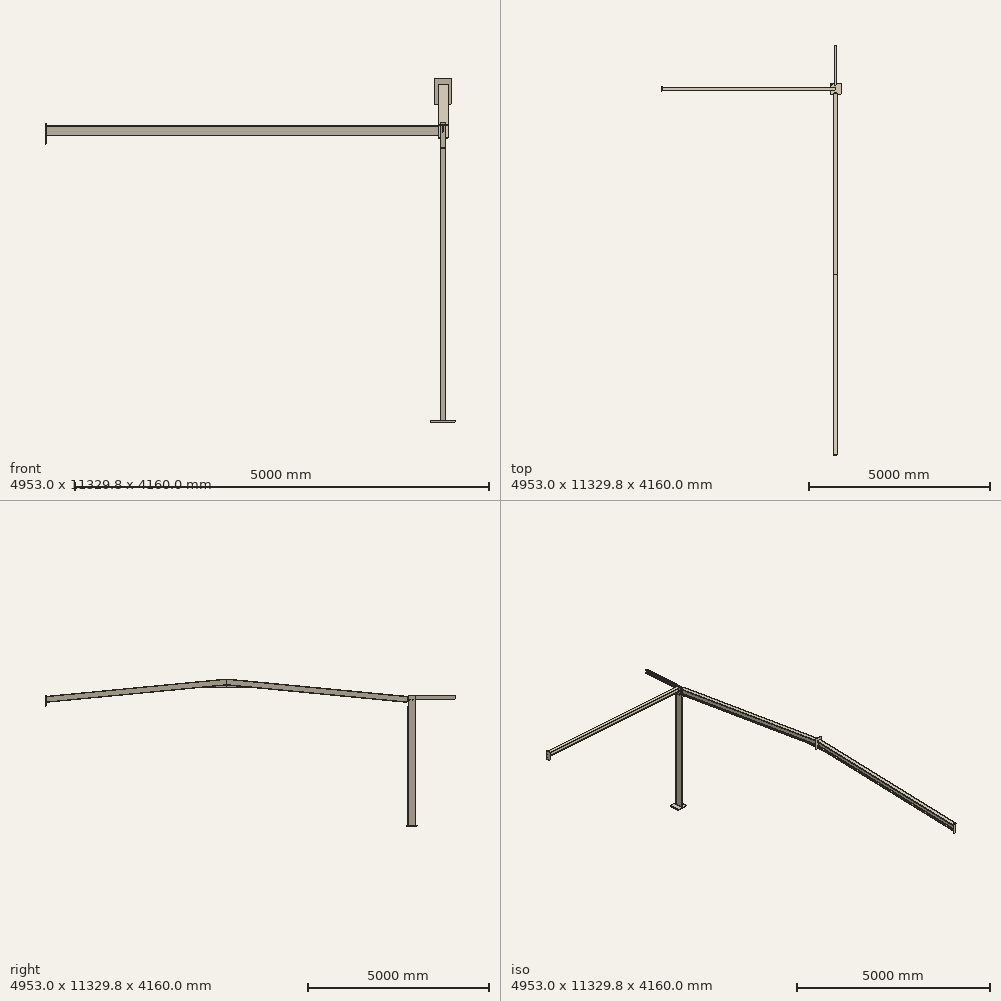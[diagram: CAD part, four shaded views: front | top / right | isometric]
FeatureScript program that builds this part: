
annotation { "Feature Type Name" : "Feature", "Feature Type Description" : "" }
export const myFeature = defineFeature(function(context is Context, id is Id, definition is map)
    precondition{}
    {
        {
            var Q0;
            Q0=qCreatedBy(makeId("Right.planeOp"),FACE);
            var sketch = newSketch(context, id + "F0", { "sketchPlane" : qUnion([Q0])});
            skLineSegment(sketch, "E0", {"start": v(-363, 0) * mm, "end": v(480.55, 0) * mm, "construction": true});
            skLineSegment(sketch, "E1", {"start": v(0, 0) * mm, "end": v(-4976.98, -479.23) * mm, "construction": true});
            skLineSegment(sketch, "E2", {"start": v(0, 0) * mm, "end": v(-23.08, 239.68) * mm, "construction": true});
            skLineSegment(sketch, "E3", {"start": v(0, 0) * mm, "end": v(4976.98, -479.23) * mm, "construction": true});
            skLineSegment(sketch, "E4", {"start": v(0, 0) * mm, "end": v(23.08, 239.68) * mm, "construction": true});
            skLineSegment(sketch, "E5.0", {"start": v(4976.98, -479.23) * mm, "end": v(5000.06, -239.54) * mm});
            skLineSegment(sketch, "E6.0", {"start": v(-4976.98, -479.23) * mm, "end": v(-5000.06, -239.54) * mm});
            skPoint(sketch, "E7.orphan", {"position": v(480.55, -46.27) * mm});
            skSolve(sketch);
        }
        {
            var Q0;
            Q0=sQuery(id+"F0.wireOp",EDGE,"E2");
            cPlane(context, id + "F1", {"entities" : qUnion([Q0]), "cplaneType" : CPlaneType.LINE_ANGLE, "offset" : 25 * mm, "angle" : 90 * degree, "width" : 150 * mm, "height" : 150 * mm});
        }
        {
            var Q0;
            Q0=sQuery(id+"F0.wireOp",EDGE,"E4");
            cPlane(context, id + "F2", {"entities" : qUnion([Q0]), "cplaneType" : CPlaneType.LINE_ANGLE, "offset" : 25 * mm, "angle" : 90 * degree, "width" : 150 * mm, "height" : 150 * mm});
        }
        {
            var Q0;
            Q0=qCreatedBy(makeId("Front.planeOp"),FACE);
            var sketch = newSketch(context, id + "F3", { "sketchPlane" : qUnion([Q0])});
            skLineSegment(sketch, "E8.bottom", {"start": v(100, -160) * mm, "end": v(-100, -160) * mm});
            skLineSegment(sketch, "E8.top", {"start": v(100, 160) * mm, "end": v(-100, 160) * mm});
            skLineSegment(sketch, "E8.left", {"start": v(100, -160) * mm, "end": v(100, 160) * mm});
            skLineSegment(sketch, "E8.right", {"start": v(-100, -160) * mm, "end": v(-100, 160) * mm});
            skPoint(sketch, "E8.middle", {"position": v(0, 0) * mm});
            skSolve(sketch);
        }
        {
            var Q0;
            Q0=qCreatedBy(id+"F1.planeOp",FACE);
            cPlane(context, id + "F4", {"entities" : qUnion([Q0]), "cplaneType" : CPlaneType.OFFSET, "offset" : 5000 * mm, "oppositeDirection" : true, "width" : 150 * mm, "height" : 150 * mm});
        }
        {
            var Q0;
            Q0=qCreatedBy(id+"F2.planeOp",FACE);
            cPlane(context, id + "F5", {"entities" : qUnion([Q0]), "cplaneType" : CPlaneType.OFFSET, "offset" : 5020 * mm, "width" : 150 * mm, "height" : 150 * mm});
        }
        {
            var Q0;
            Q0=qCreatedBy(id+"F5.planeOp",FACE);
            var sketch = newSketch(context, id + "F6", { "sketchPlane" : qUnion([Q0])});
            skLineSegment(sketch, "E9", {"start": v(60, 82.46) * mm, "end": v(-60, 82.46) * mm});
            skLineSegment(sketch, "E10", {"start": v(-60, 82.46) * mm, "end": v(-60, 72.46) * mm});
            skLineSegment(sketch, "E11", {"start": v(-60, 72.46) * mm, "end": v(-5, 72.46) * mm});
            skLineSegment(sketch, "E12", {"start": v(-5, 72.46) * mm, "end": v(-5, -72.46) * mm});
            skLineSegment(sketch, "E13", {"start": v(-5, -72.46) * mm, "end": v(-60, -72.46) * mm});
            skLineSegment(sketch, "E14", {"start": v(-60, -72.46) * mm, "end": v(-60, -82.46) * mm});
            skLineSegment(sketch, "E15", {"start": v(-60, -82.46) * mm, "end": v(60, -82.46) * mm});
            skLineSegment(sketch, "E16", {"start": v(60, -82.46) * mm, "end": v(60, -72.46) * mm});
            skLineSegment(sketch, "E17", {"start": v(60, -72.46) * mm, "end": v(5, -72.46) * mm});
            skLineSegment(sketch, "E18", {"start": v(5, -72.46) * mm, "end": v(5, 72.46) * mm});
            skLineSegment(sketch, "E19", {"start": v(5, 72.46) * mm, "end": v(60, 72.46) * mm});
            skLineSegment(sketch, "E20", {"start": v(60, 72.46) * mm, "end": v(60, 82.46) * mm});
            skPoint(sketch, "E21", {"position": v(-322.82, 17) * mm});
            skLineSegment(sketch, "E22", {"start": v(-5, 0) * mm, "end": v(5, 0) * mm, "construction": true});
            skPoint(sketch, "E23", {"position": v(0, 0) * mm});
            skSolve(sketch);
        }
        {
            var Q0;
            Q0=qSketchRegion(id+"F3",true);
            extrude(context, id + "F7", {"entities" : qUnion([Q0]), "depth" : 10 * mm});
        }
        {
            var Q0;
            Q0=qSketchRegion(id+"F6",true);
            extrude(context, id + "F8", {"entities" : qUnion([Q0]), "operationType" : NewBodyOperationType.ADD, "endBound" : BoundingType.UP_TO_NEXT, "oppositeDirection" : true, "depth" : 25 * mm});
        }
        {
            var Q0;
            Q0=qCreatedBy(id+"F4.planeOp",FACE);
            var sketch = newSketch(context, id + "F9", { "sketchPlane" : qUnion([Q0])});
            skLineSegment(sketch, "E24", {"start": v(60, 82.46) * mm, "end": v(-60, 82.46) * mm});
            skLineSegment(sketch, "E25", {"start": v(-60, 82.46) * mm, "end": v(-60, 72.46) * mm});
            skLineSegment(sketch, "E26", {"start": v(-60, 72.46) * mm, "end": v(-5, 72.46) * mm});
            skLineSegment(sketch, "E27", {"start": v(-5, 72.46) * mm, "end": v(-5, -72.46) * mm});
            skLineSegment(sketch, "E28", {"start": v(-5, -72.46) * mm, "end": v(-60, -72.46) * mm});
            skLineSegment(sketch, "E29", {"start": v(-60, -72.46) * mm, "end": v(-60, -82.46) * mm});
            skLineSegment(sketch, "E30", {"start": v(-60, -82.46) * mm, "end": v(60, -82.46) * mm});
            skLineSegment(sketch, "E31", {"start": v(60, -82.46) * mm, "end": v(60, -72.46) * mm});
            skLineSegment(sketch, "E32", {"start": v(60, -72.46) * mm, "end": v(5, -72.46) * mm});
            skLineSegment(sketch, "E33", {"start": v(5, -72.46) * mm, "end": v(5, 72.46) * mm});
            skLineSegment(sketch, "E34", {"start": v(5, 72.46) * mm, "end": v(60, 72.46) * mm});
            skLineSegment(sketch, "E35", {"start": v(60, 72.46) * mm, "end": v(60, 82.46) * mm});
            skPoint(sketch, "E36", {"position": v(-971.4, 551) * mm});
            skLineSegment(sketch, "E37", {"start": v(-5, 0) * mm, "end": v(5, 0) * mm, "construction": true});
            skPoint(sketch, "E38", {"position": v(0, 0) * mm});
            skSolve(sketch);
        }
        {
            var Q0;
            Q0=qSketchRegion(id+"F9",true);
            extrude(context, id + "F10", {"entities" : qUnion([Q0]), "operationType" : NewBodyOperationType.ADD, "endBound" : BoundingType.UP_TO_NEXT, "depth" : 25 * mm, "hasSecondDirection" : true, "secondDirectionOppositeDirection" : true, "secondDirectionDepth" : 25 * mm});
        }
        {
            var Q0;
            Q0=qCreatedBy(makeId("Top.planeOp"),FACE);
            cPlane(context, id + "F11", {"entities" : qUnion([Q0]), "cplaneType" : CPlaneType.OFFSET, "offset" : 4000 * mm, "oppositeDirection" : true, "width" : 150 * mm, "height" : 150 * mm});
        }
        {
            var Q0;
            Q0=qCreatedBy(id+"F11.planeOp",FACE);
            var sketch = newSketch(context, id + "F12", { "sketchPlane" : qUnion([Q0])});
            skLineSegment(sketch, "E39.bottom", {"start": v(150, 5276.98) * mm, "end": v(-150, 5276.98) * mm});
            skLineSegment(sketch, "E39.top", {"start": v(150, 4976.98) * mm, "end": v(-150, 4976.98) * mm});
            skLineSegment(sketch, "E39.left", {"start": v(150, 5276.98) * mm, "end": v(150, 4976.98) * mm});
            skLineSegment(sketch, "E39.right", {"start": v(-150, 5276.98) * mm, "end": v(-150, 4976.98) * mm});
            skLineSegment(sketch, "E40", {"start": v(150, 4976.98) * mm, "end": v(-150, 5276.98) * mm, "construction": true});
            skPoint(sketch, "E41", {"position": v(0, 4976.98) * mm});
            skSolve(sketch);
        }
        {
            var Q0;
            Q0=qSketchRegion(id+"F12",true);
            extrude(context, id + "F13", {"entities" : qUnion([Q0]), "depth" : 25 * mm});
        }
        {
            var Q0;
            Q0=makeQuery(id+"F13.opExtrude","CAP_FACE",FACE,{"disambiguationData":[OSD([sQuery(id+"F12.wireOp",EDGE,"E39.bottom"),sQuery(id+"F12.wireOp",EDGE,"E39.top"),sQuery(id+"F12.wireOp",EDGE,"E39.left"),sQuery(id+"F12.wireOp",EDGE,"E39.right")])],"isStart":false});
            var sketch = newSketch(context, id + "F14", { "sketchPlane" : qUnion([Q0])});
            skLineSegment(sketch, "E42", {"start": v(25.6, 5220.06) * mm, "end": v(-25.6, 5220.06) * mm});
            skLineSegment(sketch, "E43", {"start": v(-25.6, 5220.06) * mm, "end": v(-25.6, 5212.06) * mm});
            skLineSegment(sketch, "E44", {"start": v(-25.6, 5212.06) * mm, "end": v(-3, 5212.06) * mm});
            skLineSegment(sketch, "E45", {"start": v(-3, 5212.06) * mm, "end": v(-3, 5008.06) * mm});
            skLineSegment(sketch, "E46", {"start": v(-3, 5008.06) * mm, "end": v(-25.6, 5008.06) * mm});
            skLineSegment(sketch, "E47", {"start": v(-25.6, 5008.06) * mm, "end": v(-25.6, 5000.06) * mm});
            skLineSegment(sketch, "E48", {"start": v(-25.6, 5000.06) * mm, "end": v(25.6, 5000.06) * mm});
            skLineSegment(sketch, "E49", {"start": v(25.6, 5000.06) * mm, "end": v(25.6, 5008.06) * mm});
            skPoint(sketch, "E49.endSnap0", {"position": v(-14.3, 5008.06) * mm});
            skLineSegment(sketch, "E50", {"start": v(25.6, 5008.06) * mm, "end": v(3, 5008.06) * mm});
            skLineSegment(sketch, "E51", {"start": v(3, 5008.06) * mm, "end": v(3, 5212.06) * mm});
            skLineSegment(sketch, "E52", {"start": v(3, 5212.06) * mm, "end": v(25.6, 5212.06) * mm});
            skLineSegment(sketch, "E53", {"start": v(25.6, 5212.06) * mm, "end": v(25.6, 5220.06) * mm});
            skPoint(sketch, "E54", {"position": v(0, 5000.06) * mm});
            skSolve(sketch);
        }
        {
            var Q0;
            Q0=qSketchRegion(id+"F14",true);
            extrude(context, id + "F15", {"entities" : qUnion([Q0]), "operationType" : NewBodyOperationType.ADD, "depth" : 3600 * mm});
        }
        {
            var Q0;
            Q0=makeQuery(id+"F15.opExtrude","SWEPT_FACE",FACE,{"disambiguationData":[OSD([sQuery(id+"F14.wireOp",EDGE,"E42")])]});
            var sketch = newSketch(context, id + "F16", { "sketchPlane" : qUnion([Q0])});
            skLineSegment(sketch, "E55", {"start": v(25, -379.23) * mm, "end": v(-25, -379.23) * mm});
            skLineSegment(sketch, "E56", {"start": v(-25, -379.23) * mm, "end": v(-25, -479.23) * mm});
            skLineSegment(sketch, "E57", {"start": v(-25, -479.23) * mm, "end": v(25, -479.23) * mm});
            skLineSegment(sketch, "E58", {"start": v(25, -479.23) * mm, "end": v(25, -469.23) * mm});
            skLineSegment(sketch, "E59", {"start": v(25, -469.23) * mm, "end": v(-19, -469.23) * mm});
            skLineSegment(sketch, "E60", {"start": v(-19, -469.23) * mm, "end": v(-19, -389.23) * mm});
            skLineSegment(sketch, "E61", {"start": v(-19, -389.23) * mm, "end": v(25, -389.23) * mm});
            skLineSegment(sketch, "E62", {"start": v(25, -389.23) * mm, "end": v(25, -379.23) * mm});
            skPoint(sketch, "E63", {"position": v(0, -479.23) * mm});
            skSolve(sketch);
        }
        {
            var Q0;
            Q0=qSketchRegion(id+"F16",true);
            extrude(context, id + "F17", {"entities" : qUnion([Q0]), "operationType" : NewBodyOperationType.ADD, "depth" : 1100 * mm});
        }
        {
            var Q0;
            Q0=makeQuery(id+"F15.opExtrude","SWEPT_FACE",FACE,{"disambiguationData":[OSD([sQuery(id+"F14.wireOp",EDGE,"E45")])]});
            var sketch = newSketch(context, id + "F18", { "sketchPlane" : qUnion([Q0])});
            skLineSegment(sketch, "E64.bottom", {"start": v(-5175.06, -385) * mm, "end": v(-5045.06, -385) * mm});
            skLineSegment(sketch, "E64.top", {"start": v(-5175.06, -635) * mm, "end": v(-5045.06, -635) * mm});
            skLineSegment(sketch, "E64.left", {"start": v(-5175.06, -385) * mm, "end": v(-5175.06, -635) * mm});
            skLineSegment(sketch, "E64.right", {"start": v(-5045.06, -385) * mm, "end": v(-5045.06, -635) * mm});
            skPoint(sketch, "E65", {"position": v(-5110.06, -385) * mm});
            skSolve(sketch);
        }
        {
            var Q0;
            Q0=makeQuery(id+"F15.opExtrude","SWEPT_FACE",FACE,{"disambiguationData":[OSD([sQuery(id+"F14.wireOp",EDGE,"E45")])]});
            var sketch = newSketch(context, id + "F19", { "sketchPlane" : qUnion([Q0])});
            skLineSegment(sketch, "E66", {"start": v(-5153.56, -414) * mm, "end": v(-5066.56, -414) * mm});
            skLineSegment(sketch, "E67", {"start": v(-5066.56, -414) * mm, "end": v(-5066.56, -420) * mm});
            skLineSegment(sketch, "E68", {"start": v(-5066.56, -420) * mm, "end": v(-5107.06, -420) * mm});
            skLineSegment(sketch, "E69", {"start": v(-5107.06, -420) * mm, "end": v(-5107.06, -529) * mm});
            skLineSegment(sketch, "E70", {"start": v(-5107.06, -529) * mm, "end": v(-5066.56, -529) * mm});
            skLineSegment(sketch, "E71", {"start": v(-5066.56, -529) * mm, "end": v(-5066.56, -535) * mm});
            skLineSegment(sketch, "E72", {"start": v(-5066.56, -535) * mm, "end": v(-5153.56, -535) * mm});
            skLineSegment(sketch, "E73", {"start": v(-5153.56, -535) * mm, "end": v(-5153.56, -529) * mm});
            skLineSegment(sketch, "E74", {"start": v(-5153.56, -529) * mm, "end": v(-5113.06, -529) * mm});
            skLineSegment(sketch, "E75", {"start": v(-5113.06, -529) * mm, "end": v(-5113.06, -420) * mm});
            skLineSegment(sketch, "E76", {"start": v(-5113.06, -420) * mm, "end": v(-5153.56, -420) * mm});
            skLineSegment(sketch, "E77", {"start": v(-5153.56, -420) * mm, "end": v(-5153.56, -414) * mm});
            skPoint(sketch, "E78", {"position": v(-5110.06, -535) * mm});
            skSolve(sketch);
        }
        {
            var Q0;
            Q0=qSketchRegion(id+"F19",true);
            extrude(context, id + "F20", {"entities" : qUnion([Q0]), "operationType" : NewBodyOperationType.ADD, "depth" : 4800 * mm});
        }
        {
            var Q0;
            Q0=qSketchRegion(id+"F18",true);
            extrude(context, id + "F21", {"entities" : qUnion([Q0]), "depth" : 10 * mm});
        }
        {
            var Q0;
            Q0=makeQuery(id+"F15.opExtrude","SWEPT_FACE",FACE,{"disambiguationData":[OSD([sQuery(id+"F14.wireOp",EDGE,"E48")])]});
            var sketch = newSketch(context, id + "F22", { "sketchPlane" : qUnion([Q0])});
            skLineSegment(sketch, "E79.bottom", {"start": v(-82.33, -365) * mm, "end": v(87.67, -365) * mm});
            skLineSegment(sketch, "E79.top", {"start": v(-82.33, -568.21) * mm, "end": v(87.67, -568.21) * mm});
            skLineSegment(sketch, "E79.left", {"start": v(-82.33, -365) * mm, "end": v(-82.33, -568.21) * mm});
            skLineSegment(sketch, "E79.right", {"start": v(87.67, -365) * mm, "end": v(87.67, -568.21) * mm});
            skSolve(sketch);
        }
        {
            var Q0;
            Q0=qSketchRegion(id+"F22",true);
            extrude(context, id + "F23", {"entities" : qUnion([Q0]), "depth" : 15 * mm, "hasSecondDirection" : true, "secondDirectionOppositeDirection" : true, "secondDirectionDepth" : 25 * mm});
        }
        {
            var Q0;
            Q0=makeQuery(id+"F23.opExtrude","SWEPT_BODY",BODY,{"disambiguationData":[OSD([sQuery(id+"F22.wireOp",EDGE,"E79.bottom"),sQuery(id+"F22.wireOp",EDGE,"E79.top"),sQuery(id+"F22.wireOp",EDGE,"E79.left"),sQuery(id+"F22.wireOp",EDGE,"E79.right")])]});
            var Q1;
            Q1=makeQuery(id+"F7.opExtrude","SWEPT_BODY",BODY,{"disambiguationData":[OSD([sQuery(id+"F3.wireOp",EDGE,"E8.bottom"),sQuery(id+"F3.wireOp",EDGE,"E8.top"),sQuery(id+"F3.wireOp",EDGE,"E8.left"),sQuery(id+"F3.wireOp",EDGE,"E8.right")])]});
            booleanBodies(context, id + "F24", {"operationType" : BooleanOperationType.SUBTRACTION, "tools" : qUnion([Q0]), "targets" : qUnion([Q1])});
        }
        {
            var Q0;
            Q0=makeQuery(id+"F15.opExtrude","SWEPT_FACE",FACE,{"disambiguationData":[OSD([sQuery(id+"F14.wireOp",EDGE,"E48")])]});
            var sketch = newSketch(context, id + "F25", { "sketchPlane" : qUnion([Q0])});
            skLineSegment(sketch, "E80.bottom", {"start": v(-25.6, -375) * mm, "end": v(25.6, -375) * mm});
            skLineSegment(sketch, "E80.top", {"start": v(-25.6, -675) * mm, "end": v(25.6, -675) * mm});
            skLineSegment(sketch, "E80.left", {"start": v(-25.6, -375) * mm, "end": v(-25.6, -675) * mm});
            skLineSegment(sketch, "E80.right", {"start": v(25.6, -375) * mm, "end": v(25.6, -675) * mm});
            skSolve(sketch);
        }
        {
            var Q0;
            Q0=qSketchRegion(id+"F25",true);
            extrude(context, id + "F26", {"entities" : qUnion([Q0]), "depth" : 15 * mm});
        }
        {
            var Q0;
            Q0=makeQuery(id+"F13.opExtrude","SWEPT_BODY",BODY,{"disambiguationData":[OSD([sQuery(id+"F12.wireOp",EDGE,"E39.bottom"),sQuery(id+"F12.wireOp",EDGE,"E39.top"),sQuery(id+"F12.wireOp",EDGE,"E39.left"),sQuery(id+"F12.wireOp",EDGE,"E39.right")])]});
            var Q1;
            Q1=makeQuery(id+"F26.opExtrude","SWEPT_BODY",BODY,{"disambiguationData":[OSD([sQuery(id+"F25.wireOp",EDGE,"E80.bottom"),sQuery(id+"F25.wireOp",EDGE,"E80.top"),sQuery(id+"F25.wireOp",EDGE,"E80.left"),sQuery(id+"F25.wireOp",EDGE,"E80.right")])]});
            var Q2;
            Q2=qCreatedBy(makeId("Front.planeOp"),FACE);
            mirror(context, id + "F27", {"entities" : qUnion([Q0, Q1]), "mirrorPlane" : qUnion([Q2])});
        }
        {
            var Q0;
            Q0=makeQuery(id+"F20.opExtrude","CAP_FACE",FACE,{"disambiguationData":[OSD([sQuery(id+"F19.wireOp",EDGE,"E66"),sQuery(id+"F19.wireOp",EDGE,"E67"),sQuery(id+"F19.wireOp",EDGE,"E68"),sQuery(id+"F19.wireOp",EDGE,"E69"),sQuery(id+"F19.wireOp",EDGE,"E70"),sQuery(id+"F19.wireOp",EDGE,"E71"),sQuery(id+"F19.wireOp",EDGE,"E72"),sQuery(id+"F19.wireOp",EDGE,"E73"),sQuery(id+"F19.wireOp",EDGE,"E74"),sQuery(id+"F19.wireOp",EDGE,"E75"),sQuery(id+"F19.wireOp",EDGE,"E76"),sQuery(id+"F19.wireOp",EDGE,"E77")])],"isStart":false});
            var sketch = newSketch(context, id + "F28", { "sketchPlane" : qUnion([Q0])});
            skCircle(sketch, "E81", {"center": v(-5153.06, -399.15) * mm, "radius": 9 * mm});
            skLineSegment(sketch, "E82", {"start": v(-5110.06, -414) * mm, "end": v(-5110.06, -359.35) * mm, "construction": true});
            skPoint(sketch, "E82.endSnap0", {"position": v(-5110.06, -414) * mm});
            skCircle(sketch, "E83.MirrorC", {"center": v(-5067.06, -399.15) * mm, "radius": 9 * mm});
            skCircle(sketch, "E84.0.1.0", {"center": v(-5067.54, -499.15) * mm, "radius": 9 * mm});
            skCircle(sketch, "E84.0.1.1", {"center": v(-5153.54, -499.15) * mm, "radius": 9 * mm});
            skCircle(sketch, "E84.0.2.0", {"center": v(-5068.02, -599.15) * mm, "radius": 9 * mm});
            skCircle(sketch, "E84.0.2.1", {"center": v(-5154.02, -599.15) * mm, "radius": 9 * mm});
            skLineSegment(sketch, "E84.direction1", {"start": v(-5067.06, -399.15) * mm, "end": v(-5039.06, -399.15) * mm, "construction": true});
            skLineSegment(sketch, "E84.direction2", {"start": v(-5067.06, -399.15) * mm, "end": v(-5067.54, -499.15) * mm, "construction": true});
            skSolve(sketch);
        }
        {
            var Q0;
            Q0=qSketchRegion(id+"F28",true);
            extrude(context, id + "F29", {"entities" : qUnion([Q0]), "operationType" : NewBodyOperationType.REMOVE, "endBound" : BoundingType.THROUGH_ALL, "oppositeDirection" : true, "depth" : 25 * mm});
        }
        {
            var Q0;
            Q0=makeQuery(id+"F13.opExtrude","CAP_FACE",FACE,{"disambiguationData":[OSD([sQuery(id+"F12.wireOp",EDGE,"E39.bottom"),sQuery(id+"F12.wireOp",EDGE,"E39.top"),sQuery(id+"F12.wireOp",EDGE,"E39.left"),sQuery(id+"F12.wireOp",EDGE,"E39.right")])],"isStart":false});
            var sketch = newSketch(context, id + "F30", { "sketchPlane" : qUnion([Q0])});
            skCircle(sketch, "E85", {"center": v(110, 5236.98) * mm, "radius": 12 * mm});
            skLineSegment(sketch, "E86", {"start": v(150, 5126.98) * mm, "end": v(192.32, 5126.98) * mm, "construction": true});
            skLineSegment(sketch, "E87", {"start": v(0, 5276.98) * mm, "end": v(0, 5382.82) * mm, "construction": true});
            skCircle(sketch, "E88.MirrorC", {"center": v(110, 5016.98) * mm, "radius": 12 * mm});
            skCircle(sketch, "E89.MirrorC", {"center": v(-110, 5236.98) * mm, "radius": 12 * mm});
            skCircle(sketch, "E90.MirrorC", {"center": v(-110, 5016.98) * mm, "radius": 12 * mm});
            skSolve(sketch);
        }
        {
            var Q0;
            Q0=qSketchRegion(id+"F30",true);
            extrude(context, id + "F31", {"entities" : qUnion([Q0]), "operationType" : NewBodyOperationType.REMOVE, "oppositeDirection" : true, "depth" : 40 * mm});
        }
        {
            var Q0;
            Q0=makeQuery(id+"F20.opExtrude","SWEPT_FACE",FACE,{"disambiguationData":[OSD([sQuery(id+"F19.wireOp",EDGE,"E66")])]});
            var sketch = newSketch(context, id + "F32", { "sketchPlane" : qUnion([Q0])});
            skLineSegment(sketch, "E91", {"start": v(-2403, 5153.56) * mm, "end": v(-2403, 4659.05) * mm, "construction": true});
            skSolve(sketch);
        }
        {
            var Q0;
            Q0=sQuery(id+"F32.wireOp",EDGE,"E91");
            cPlane(context, id + "F33", {"entities" : qUnion([Q0]), "cplaneType" : CPlaneType.LINE_ANGLE, "offset" : 25 * mm, "angle" : 90 * degree, "width" : 150 * mm, "height" : 150 * mm});
        }
        {
            var Q0;
            Q0=makeQuery(id+"F21.opExtrude","SWEPT_BODY",BODY,{"disambiguationData":[OSD([sQuery(id+"F18.wireOp",EDGE,"E64.bottom"),sQuery(id+"F18.wireOp",EDGE,"E64.top"),sQuery(id+"F18.wireOp",EDGE,"E64.left"),sQuery(id+"F18.wireOp",EDGE,"E64.right")])]});
            var Q1;
            Q1=qCreatedBy(id+"F33.planeOp",FACE);
            mirror(context, id + "F34", {"operationType" : NewBodyOperationType.ADD, "entities" : qUnion([Q0]), "mirrorPlane" : qUnion([Q1])});
        }
        {
            var Q0;
            Q0=makeQuery(id+"F7.opExtrude","SWEPT_FACE",FACE,{"disambiguationData":[OSD([sQuery(id+"F3.wireOp",EDGE,"E8.top")])]});
            var sketch = newSketch(context, id + "F35", { "sketchPlane" : qUnion([Q0])});
            skLineSegment(sketch, "E92", {"start": v(0, 0) * mm, "end": v(0, -69.19) * mm, "construction": true});
            skPoint(sketch, "E92.endSnap0", {"position": v(0, -10) * mm});
            skSolve(sketch);
        }
        {
            var Q0;
            Q0=sQuery(id+"F35.wireOp",EDGE,"E92");
            cPlane(context, id + "F36", {"entities" : qUnion([Q0]), "cplaneType" : CPlaneType.LINE_ANGLE, "offset" : 25 * mm, "angle" : 90 * degree, "width" : 150 * mm, "height" : 150 * mm});
        }
        {
            var Q0;
            Q0=qCreatedBy(id+"F36.planeOp",FACE);
            var sketch = newSketch(context, id + "F37", { "sketchPlane" : qUnion([Q0])});
            skLineSegment(sketch, "E93", {"start": v(0, -154.79) * mm, "end": v(0, -82.84) * mm});
            skLineSegment(sketch, "E94", {"start": v(0, -82.84) * mm, "end": v(771.44, -154.79) * mm});
            skLineSegment(sketch, "E95", {"start": v(0, -154.79) * mm, "end": v(771.44, -154.79) * mm});
            skSolve(sketch);
        }
        {
            var Q0;
            Q0=qSketchRegion(id+"F37",true);
            extrude(context, id + "F38", {"entities" : qUnion([Q0]), "depth" : 5 * mm, "hasSecondDirection" : true, "secondDirectionOppositeDirection" : true, "secondDirectionDepth" : 5 * mm});
        }
        {
            var Q0;
            Q0=makeQuery(id+"F38.opExtrude","SWEPT_BODY",BODY,{"disambiguationData":[OSD([sQuery(id+"F37.wireOp",EDGE,"E93"),sQuery(id+"F37.wireOp",EDGE,"E94"),sQuery(id+"F37.wireOp",EDGE,"E95")])]});
            var Q1;
            Q1=qCreatedBy(makeId("Front.planeOp"),FACE);
            mirror(context, id + "F39", {"entities" : qUnion([Q0]), "mirrorPlane" : qUnion([Q1])});
        }
        {
            var Q0;
            Q0=makeQuery(id+"F26.opExtrude","CAP_FACE",FACE,{"disambiguationData":[OSD([sQuery(id+"F25.wireOp",EDGE,"E80.bottom"),sQuery(id+"F25.wireOp",EDGE,"E80.top"),sQuery(id+"F25.wireOp",EDGE,"E80.left"),sQuery(id+"F25.wireOp",EDGE,"E80.right")])],"isStart":false});
            var sketch = newSketch(context, id + "F40", { "sketchPlane" : qUnion([Q0])});
            skLineSegment(sketch, "E96.bottom", {"start": v(-97.7, -332.78) * mm, "end": v(130.9, -332.78) * mm});
            skLineSegment(sketch, "E96.top", {"start": v(-97.7, -687.38) * mm, "end": v(130.9, -687.38) * mm});
            skLineSegment(sketch, "E96.left", {"start": v(-97.7, -332.78) * mm, "end": v(-97.7, -687.38) * mm});
            skLineSegment(sketch, "E96.right", {"start": v(130.9, -332.78) * mm, "end": v(130.9, -687.38) * mm});
            skSolve(sketch);
        }
        {
            var Q0;
            Q0 = qSketchRegion(id + "F40", true);
            extrude(context, id + "F41", {"entities" : qUnion([Q0]), "oppositeDirection" : true, "depth" : 50 * mm});
        }
        {
            var Q0;
            Q0=makeQuery(id+"F41.opExtrude","SWEPT_BODY",BODY,{"disambiguationData":[OSD([sQuery(id+"F40.wireOp",EDGE,"E96.bottom"),sQuery(id+"F40.wireOp",EDGE,"E96.top"),sQuery(id+"F40.wireOp",EDGE,"E96.left"),sQuery(id+"F40.wireOp",EDGE,"E96.right")])]});
            var Q1;
            Q1=makeQuery(id+"F7.opExtrude","SWEPT_BODY",BODY,{"disambiguationData":[OSD([sQuery(id+"F3.wireOp",EDGE,"E8.bottom"),sQuery(id+"F3.wireOp",EDGE,"E8.top"),sQuery(id+"F3.wireOp",EDGE,"E8.left"),sQuery(id+"F3.wireOp",EDGE,"E8.right")])]});
            booleanBodies(context, id + "F42", {"operationType" : BooleanOperationType.SUBTRACTION, "tools" : qUnion([Q0]), "targets" : qUnion([Q1])});
        }
    });
